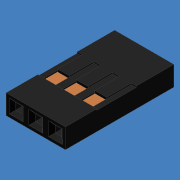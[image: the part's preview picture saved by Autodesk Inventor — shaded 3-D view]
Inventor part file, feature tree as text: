
AUTODESK INVENTOR PART (.ipt)
format: ipt  version: 2012 (Build 160160000, 160)  size: 218,112 bytes
history: native  units: mm (DEFAULTED — no unit token found)
features: extrude x6, sketch x6, projected_geometry x4
ambient origin geometry x8: Origin, YZ Plane, XZ Plane, XY Plane, X Axis, Y Axis, Z Axis, Center Point
bodies: Solid1 (feature_tree)
feature tree (16):
  extrude  "Extrusion1"  Depth=7.62mm
  extrude  "Extrusion2"  Depth=0.381mm
  extrude  "Extrusion3"  Depth=0.381mm
  extrude  "Extrusion4"  Depth=1.778mm
  sketch  "Sketch5"  dims[d9=1.778mm d10=0.762mm]
  extrude  "Extrusion6"  Depth=0.762mm
  extrude  "Extrusion7"  Depth=0.381mm
  sketch  "Sketch6"  dims[d11=0.762mm d12=0.381mm d13=-8.726646mm d14=2.54mm d15=0.0mm d16=1.905mm d17=3.175mm d18=0.0mm d19=5.08mm d21=1.524mm d23=0.889mm d24=0.889mm d25=0.635mm d30=3.175mm d31=4.064mm d32=0.3175mm d33=0.0mm d34=0.15875mm d35=0.0mm]
  sketch  "Sketch1"  dims[d0=2.54mm d1=7.62mm]
  sketch  "Sketch2"  dims[d2=13.97mm d3=0.0mm d4=0.381mm]
  sketch  "Sketch3"  dims[d5=0.381mm d6=0.381mm]
  projected_geometry  "Projected Loop1"
  projected_geometry  "Projected Loop2"
  sketch  "Sketch4"  dims[d7=1.778mm d8=1.778mm]
  projected_geometry  "Projected Loop3"
  projected_geometry  "Projected Loop4"
